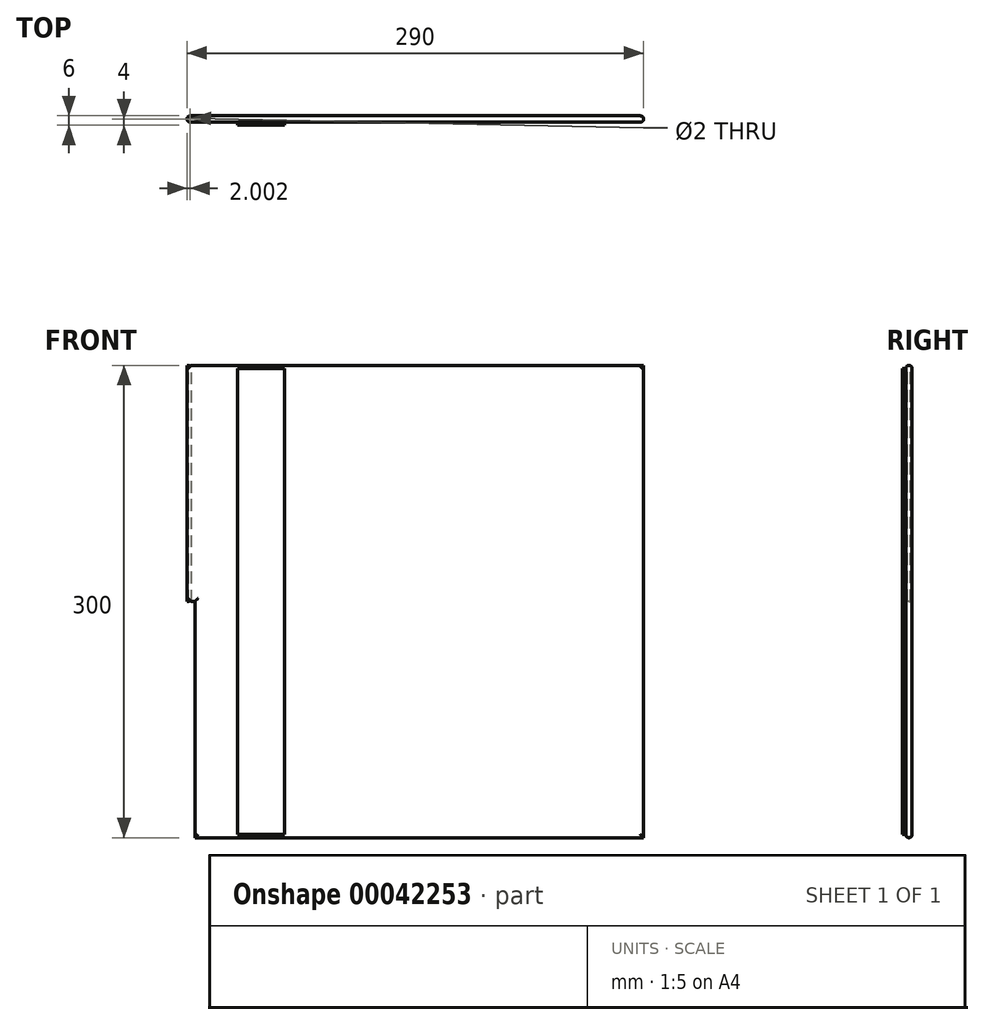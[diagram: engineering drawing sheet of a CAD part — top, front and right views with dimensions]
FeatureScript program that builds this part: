
annotation { "Feature Type Name" : "Feature", "Feature Type Description" : "" }
export const myFeature = defineFeature(function(context is Context, id is Id, definition is map)
    precondition{}
    {
        {
            var Q0;
            Q0=qCreatedBy(makeId("Front.planeOp"),FACE);
            var sketch = newSketch(context, id + "F0", { "sketchPlane" : qUnion([Q0])});
            skLineSegment(sketch, "E0.bottom", {"start": v(-38.59, 250.85) * mm, "end": v(251.41, 250.85) * mm});
            skLineSegment(sketch, "E0.right", {"start": v(251.41, 250.85) * mm, "end": v(251.41, -49.15) * mm});
            skLineSegment(sketch, "E1", {"start": v(-38.59, 250.85) * mm, "end": v(-38.59, 100.85) * mm});
            skLineSegment(sketch, "E2", {"start": v(-38.59, 100.85) * mm, "end": v(-33.59, 100.85) * mm});
            skLineSegment(sketch, "E3", {"start": v(-33.59, 100.85) * mm, "end": v(-33.59, -49.15) * mm});
            skLineSegment(sketch, "E4", {"start": v(-33.59, -49.15) * mm, "end": v(251.41, -49.15) * mm});
            skSolve(sketch);
        }
        {
            var Q0;
            Q0=qSketchRegion(id+"F0",true);
            extrude(context, id + "F1", {"entities" : qUnion([Q0]), "depth" : 4 * mm});
        }
        {
            var Q0;
            Q0=makeQuery(id+"F1.opExtrude","SWEPT_FACE",FACE,{"disambiguationData":[OSD([sQuery(id+"F0.wireOp",EDGE,"E0.bottom")])]});
            var sketch = newSketch(context, id + "F2", { "sketchPlane" : qUnion([Q0])});
            skLineSegment(sketch, "E5", {"start": v(-38.59, 0) * mm, "end": v(-34.59, 0) * mm, "construction": true});
            skLineSegment(sketch, "E6", {"start": v(-34.59, 0) * mm, "end": v(-34.59, -4) * mm, "construction": true});
            skLineSegment(sketch, "E7", {"start": v(-38.59, -4) * mm, "end": v(-34.59, 0) * mm, "construction": true});
            skCircle(sketch, "E8", {"center": v(-36.59, -2) * mm, "radius": 1 * mm});
            skSolve(sketch);
        }
        {
            var Q0;
            Q0=qSketchRegion(id+"F2",true);
            extrude(context, id + "F3", {"entities" : qUnion([Q0]), "operationType" : NewBodyOperationType.REMOVE, "oppositeDirection" : true, "depth" : 310 * mm});
        }
        {
            var Q0;
            Q0=makeQuery(id+"F1.opExtrude","CAP_FACE",FACE,{"disambiguationData":[OSD([sQuery(id+"F0.wireOp",EDGE,"E0.bottom"),sQuery(id+"F0.wireOp",EDGE,"E0.top"),sQuery(id+"F0.wireOp",EDGE,"E0.left"),sQuery(id+"F0.wireOp",EDGE,"E0.right")])],"isStart":false});
            fillet(context, id + "F4", {"entities" : qUnion([Q0]), "radius" : 2 * mm, "tangentPropagation" : true, "allowEdgeOverflow" : false});
        }
        {
            var Q0;
            Q0=makeQuery(id+"F1.opExtrude","CAP_FACE",FACE,{"disambiguationData":[OSD([sQuery(id+"F0.wireOp",EDGE,"E0.bottom"),sQuery(id+"F0.wireOp",EDGE,"E0.top"),sQuery(id+"F0.wireOp",EDGE,"E0.left"),sQuery(id+"F0.wireOp",EDGE,"E0.right")])],"isStart":true});
            fillet(context, id + "F5", {"entities" : qUnion([Q0]), "radius" : 2 * mm, "tangentPropagation" : true, "allowEdgeOverflow" : false});
        }
        {
            var Q0;
            Q0=makeQuery(id+"F1.opExtrude","CAP_FACE",FACE,{"disambiguationData":[OSD([sQuery(id+"F0.wireOp",EDGE,"E0.bottom"),sQuery(id+"F0.wireOp",EDGE,"E0.right"),sQuery(id+"F0.wireOp",EDGE,"E1"),sQuery(id+"F0.wireOp",EDGE,"E2"),sQuery(id+"F0.wireOp",EDGE,"E3"),sQuery(id+"F0.wireOp",EDGE,"E4")])],"isStart":false});
            var sketch = newSketch(context, id + "F6", { "sketchPlane" : qUnion([Q0])});
            skLineSegment(sketch, "E9", {"start": v(-6.59, 248.85) * mm, "end": v(-6.59, -47.15) * mm});
            skLineSegment(sketch, "E10", {"start": v(-6.59, -47.15) * mm, "end": v(23.41, -47.15) * mm});
            skLineSegment(sketch, "E11", {"start": v(23.41, -47.15) * mm, "end": v(23.41, 248.85) * mm});
            skLineSegment(sketch, "E12", {"start": v(23.41, 248.85) * mm, "end": v(-6.59, 248.85) * mm});
            skSolve(sketch);
        }
        {
            var Q0;
            Q0 = qSketchRegion(id + "F6", true);
            extrude(context, id + "F7", {"entities" : qUnion([Q0]), "operationType" : NewBodyOperationType.ADD, "depth" : 2 * mm});
        }
    });
